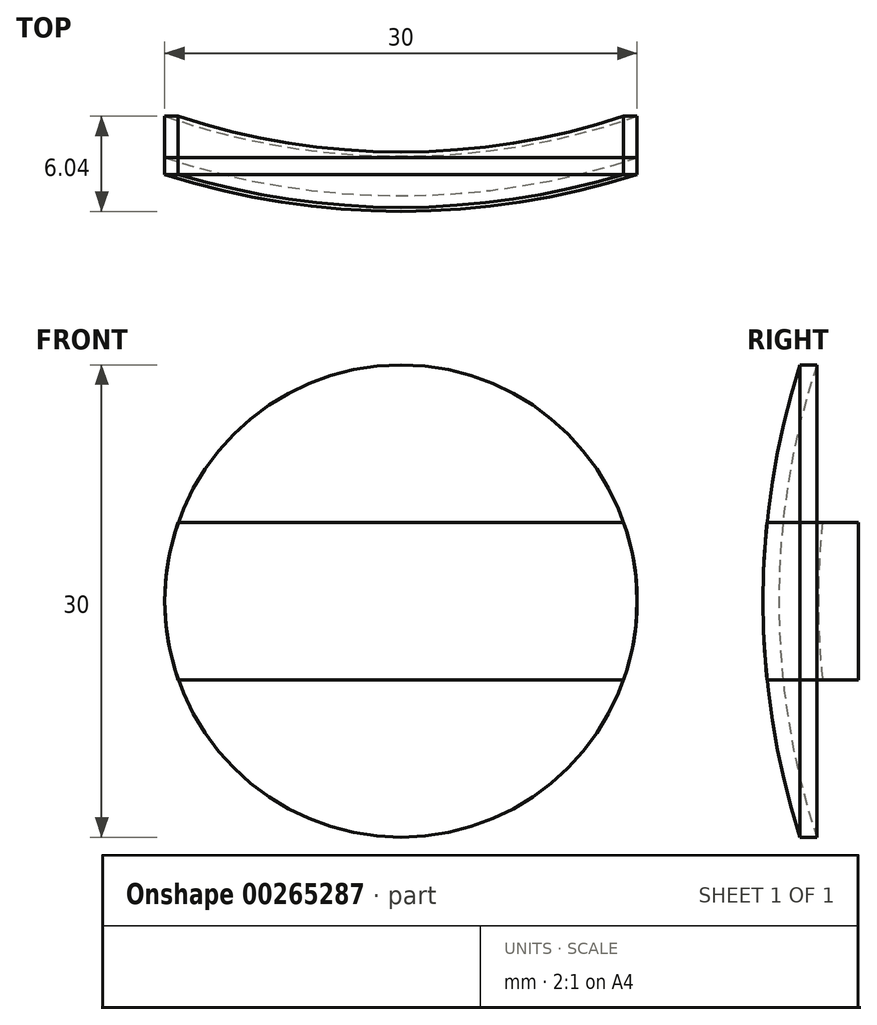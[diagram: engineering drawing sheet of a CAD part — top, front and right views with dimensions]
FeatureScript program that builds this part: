
annotation { "Feature Type Name" : "Feature", "Feature Type Description" : "" }
export const myFeature = defineFeature(function(context is Context, id is Id, definition is map)
    precondition{}
    {
        {
            var Q0;
            Q0=qCreatedBy(makeId("Front.planeOp"),FACE);
            var sketch = newSketch(context, id + "F0", { "sketchPlane" : qUnion([Q0])});
            skArc(sketch, "E0", {"start": v(0, -50) * mm, "mid": v(50, 0) * mm, "end": v(0, 50) * mm});
            skLineSegment(sketch, "E1", {"start": v(0, 50) * mm, "end": v(0, -50) * mm});
            skSolve(sketch);
        }
        {
            var Q0;
            Q0 = qSketchRegion(id + "F0", true);
            var Q1;
            Q1=sQuery(id+"F0.wireOp",EDGE,"E1");
            revolve(context, id + "F1", {"entities" : qUnion([Q0]), "axis" : qUnion([Q1]), "revolveType" : RevolveType.FULL});
        }
        {
            var Q0;
            Q0=qCreatedBy(makeId("Front.planeOp"),FACE);
            var sketch = newSketch(context, id + "F2", { "sketchPlane" : qUnion([Q0])});
            skLineSegment(sketch, "E2.bottom", {"start": v(-60, 5) * mm, "end": v(60, 5) * mm});
            skLineSegment(sketch, "E2.top", {"start": v(-60, -5) * mm, "end": v(60, -5) * mm});
            skLineSegment(sketch, "E2.left", {"start": v(-60, 5) * mm, "end": v(-60, -5) * mm});
            skLineSegment(sketch, "E2.right", {"start": v(60, 5) * mm, "end": v(60, -5) * mm});
            skSolve(sketch);
        }
        {
            var Q0;
            Q0 = qSketchRegion(id + "F2", true);
            extrude(context, id + "F3", {"entities" : qUnion([Q0]), "operationType" : NewBodyOperationType.REMOVE, "endBound" : BoundingType.SYMMETRIC, "depth" : 153 * mm});
        }
        {
            var Q0;
            Q0=makeQuery(id+"F3.boolean.opBoolean","COPY",FACE,{"derivedFrom":makeQuery(id+"F3.opExtrude","SWEPT_FACE",FACE,{"disambiguationData":[OSD([sQuery(id+"F2.wireOp",EDGE,"E2.bottom")])]})});
            var Q1;
            Q1=makeQuery(id+"F3.boolean.opBoolean","COPY",FACE,{"derivedFrom":makeQuery(id+"F3.opExtrude","SWEPT_FACE",FACE,{"disambiguationData":[OSD([sQuery(id+"F2.wireOp",EDGE,"E2.top")])]})});
            shell(context, id + "F4", {"entities" : qUnion([Q0, Q1]), "thickness" : 3 * mm});
        }
        {
            var Q0;
            Q0=qCreatedBy(makeId("Front.planeOp"),FACE);
            var sketch = newSketch(context, id + "F5", { "sketchPlane" : qUnion([Q0])});
            skCircle(sketch, "E3", {"center": v(0, 0) * mm, "radius": 15 * mm});
            skSolve(sketch);
        }
        {
            var Q0;
            Q0 = qSketchRegion(id + "F5", true);
            extrude(context, id + "F6", {"entities" : qUnion([Q0]), "operationType" : NewBodyOperationType.REMOVE, "depth" : 107.3 * mm});
        }
        {
            var Q0;
            Q0=qCreatedBy(makeId("Front.planeOp"),FACE);
            var sketch = newSketch(context, id + "F7", { "sketchPlane" : qUnion([Q0])});
            skArc(sketch, "E4", {"start": v(48.74, -5) * mm, "mid": v(49, 0) * mm, "end": v(48.74, 5) * mm});
            skArc(sketch, "E5", {"start": v(45.22, -5) * mm, "mid": v(45.5, 0) * mm, "end": v(45.22, 5) * mm});
            skPoint(sketch, "E6", {"position": v(48.74, 5) * mm});
            skPoint(sketch, "E7", {"position": v(45.22, 5) * mm});
            skPoint(sketch, "E8", {"position": v(45.22, -5) * mm});
            skPoint(sketch, "E9", {"position": v(48.74, -5) * mm});
            skLineSegment(sketch, "E10", {"start": v(45.22, 5) * mm, "end": v(48.74, 5) * mm});
            skLineSegment(sketch, "E11", {"start": v(45.22, -5) * mm, "end": v(48.74, -5) * mm});
            skLineSegment(sketch, "E12", {"start": v(0, 0) * mm, "end": v(0, 58.89) * mm});
            skSolve(sketch);
        }
        {
            var Q0;
            Q0=makeQuery(id+"F7.imprint","IMPRINT",FACE,{"disambiguationData":[TD([[makeQuery(id+"F7.imprint","IMPRINT",EDGE,{"derivedFrom":sQuery(id+"F7.wireOp",EDGE,"E4")}),1.0]])]});
            var Q1;
            Q1=sQuery(id+"F7.wireOp",EDGE,"E12");
            revolve(context, id + "F8", {"entities" : qUnion([Q0]), "axis" : qUnion([Q1]), "revolveType" : RevolveType.FULL});
        }
        {
            var Q0;
            Q0=qCreatedBy(makeId("Front.planeOp"),FACE);
            var sketch = newSketch(context, id + "F9", { "sketchPlane" : qUnion([Q0])});
            skCircle(sketch, "E13", {"center": v(0, 0) * mm, "radius": 15 * mm});
            skSolve(sketch);
        }
        {
            var Q0;
            Q0=qCreatedBy(makeId("Front.planeOp"),FACE);
            var sketch = newSketch(context, id + "F10", { "sketchPlane" : qUnion([Q0])});
            skCircle(sketch, "E14", {"center": v(0, 0) * mm, "radius": 49 * mm});
            skCircle(sketch, "E15", {"center": v(0, 0) * mm, "radius": 48 * mm});
            skLineSegment(sketch, "E16", {"start": v(0, 49) * mm, "end": v(0, -49) * mm});
            skSolve(sketch);
        }
        {
            var Q0;
            {var subQ0=sQuery(id+"F10.wireOp",EDGE,"E16");var subQ1=sQuery(id+"F10.wireOp",EDGE,"E14");var subQ2=makeQuery(id+"F10.imprint","INTERSECT",VERTEX,{"disambiguationData":[OD(0.0)],"derivedFrom":[subQ1,subQ0]});Q0=makeQuery(id+"F10.imprint","IMPRINT",FACE,{"disambiguationData":[TD([[makeQuery(id+"F10.imprint","IMPRINT",EDGE,{"disambiguationData":[TD([[subQ2,1.0]])],"derivedFrom":subQ1}),1.0]])]});}
            var Q1;
            Q1=sQuery(id+"F10.wireOp",EDGE,"E16");
            revolve(context, id + "F11", {"entities" : qUnion([Q0]), "axis" : qUnion([Q1]), "revolveType" : RevolveType.FULL});
        }
        {
            var Q0;
            Q0 = qSketchRegion(id + "F9", true);
            extrude(context, id + "F12", {"entities" : qUnion([Q0]), "operationType" : NewBodyOperationType.INTERSECT, "endBound" : BoundingType.THROUGH_ALL, "depth" : 25 * mm});
        }
    });
